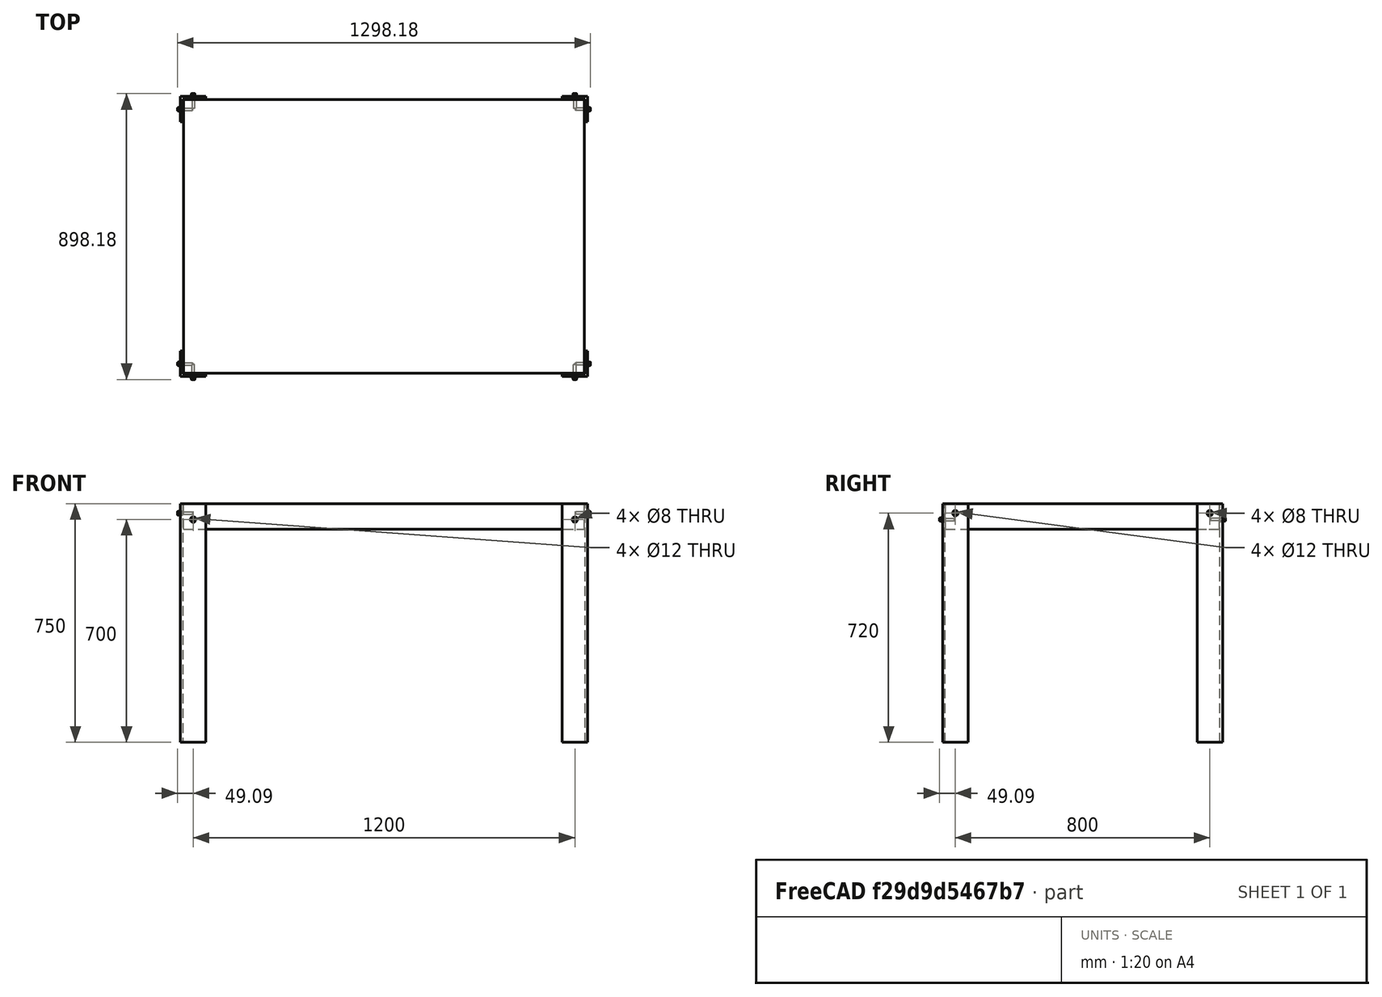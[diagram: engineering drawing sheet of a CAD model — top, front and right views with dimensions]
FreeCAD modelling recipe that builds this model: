
FCSTD DOCUMENT  (FreeCAD 0.16R6265 (Git))
Label: table
License: CreativeCommons Attribution
LicenseURL: http://creativecommons.org/licenses/by/4.0/
objects: Part::Cut×12, Part::Box×9, Part::FeaturePython×8, Part::Cylinder×4, App::DocumentObjectGroup×1
note: 33 computed .brp shape members not serialized (recipe doc carries the construction recipe); baked Part::Feature solids carry a one-line shape summary decoded from their .brp

FEATURE [Part::Box] Box  label="Cube"
  Height = 750
  Length = 80
  Width = 80
FEATURE [Part::Box] Box001  label="Cube001"
  Height = 750
  Length = 80
  Placement = pos=(8,8,0) rot=(0,0,1;0rad)
  Width = 80
FEATURE [Part::Cut] Cut
  Base = -> Box
  Tool = -> Box001
FEATURE [Part::Box] Box002  label="Cube002"
  Height = 750
  Length = 80
  Placement = pos=(0,800,0) rot=(0,0,1;0rad)
  Width = 80
FEATURE [Part::Box] Box003  label="Cube003"
  Height = 750
  Length = 80
  Placement = pos=(8,792,0) rot=(0,0,1;0rad)
  Width = 80
FEATURE [Part::Cut] Cut001
  Base = -> Box002
  Tool = -> Box003
FEATURE [Part::Box] Box004  label="Cube004"
  Height = 750
  Length = 80
  Placement = pos=(1200,0,0) rot=(0,0,1;0rad)
  Width = 80
FEATURE [Part::Box] Box005  label="Cube005"
  Height = 750
  Length = 80
  Placement = pos=(1192,8,0) rot=(0,0,1;0rad)
  Width = 80
FEATURE [Part::Cut] Cut002
  Base = -> Box004
  Tool = -> Box005
FEATURE [Part::Box] Box006  label="Cube006"
  Height = 750
  Length = 80
  Placement = pos=(1200,800,0) rot=(0,0,1;0rad)
  Width = 80
FEATURE [Part::Box] Box007  label="Cube007"
  Height = 750
  Length = 80
  Placement = pos=(1192,792,0) rot=(0,0,1;0rad)
  Width = 80
FEATURE [Part::Cut] Cut003
  Base = -> Box006
  Tool = -> Box007
FEATURE [Part::Box] Box008  label="Tabletop"
  Height = 80
  Length = 1260
  Placement = pos=(10,10,670) rot=(0,0,1;0rad)
  Width = 860
  expr: Width = 880 - 20
  expr: Length = 1280 - 20
FEATURE [Part::Cylinder] Cylinder
  Angle = 360
  Height = 1300
  Placement = pos=(-10,40,720) rot=(0,1,0;1.5708rad)
  Radius = 6
FEATURE [Part::Cylinder] Cylinder001
  Angle = 360
  Height = 1300
  Placement = pos=(-10,840,720) rot=(0,1,0;1.5708rad)
  Radius = 6
FEATURE [Part::Cylinder] Cylinder002
  Angle = 360
  Height = 900
  Placement = pos=(40,-10,700) rot=(-1,0,0;1.5708rad)
  Radius = 6
FEATURE [Part::Cylinder] Cylinder003
  Angle = 360
  Height = 900
  Placement = pos=(1240,-10,700) rot=(-1,0,0;1.5708rad)
  Radius = 6
FEATURE [Part::Cut] Cut004
  Base = -> Cut
  Tool = -> Cylinder
FEATURE [Part::Cut] Cut005
  Base = -> Cut002
  Tool = -> Cylinder
FEATURE [Part::Cut] Cut006  label="Foot 01"
  Base = -> Cut004
  Tool = -> Cylinder002
FEATURE [Part::Cut] Cut007
  Base = -> Cut001
  Tool = -> Cylinder002
FEATURE [Part::Cut] Cut008  label="Foot 02"
  Base = -> Cut007
  Tool = -> Cylinder001
FEATURE [Part::Cut] Cut009
  Base = -> Cut003
  Tool = -> Cylinder001
FEATURE [Part::Cut] Cut010  label="Foot 03"
  Base = -> Cut009
  Tool = -> Cylinder003
FEATURE [Part::Cut] Cut011  label="Foot 04"
  Base = -> Cut005
  Tool = -> Cylinder003
FEATURE [Part::FeaturePython] Screw  label="M8x40-Screw"  # Fasteners workbench fastener (typed FeaturePython)
  Placement = pos=(-2,40,720) rot=(0,-1,0;1.5708rad)
  diameter = 3
  invert = false
  length = 5
  matchOuter = false
  offset = 0
  thread = false
  type = 1
FEATURE [Part::FeaturePython] Screw001  label="M8x40-Screw001"  # Fasteners workbench fastener (typed FeaturePython)
  Placement = pos=(-2,840,720) rot=(0,-1,0;1.5708rad)
  diameter = 3
  invert = false
  length = 5
  matchOuter = false
  offset = 0
  thread = false
  type = 1
FEATURE [Part::FeaturePython] Screw002  label="M8x40-Screw002"  # Fasteners workbench fastener (typed FeaturePython)
  Placement = pos=(1282,40,720) rot=(0,1,0;1.5708rad)
  diameter = 3
  invert = false
  length = 5
  matchOuter = false
  offset = 0
  thread = false
  type = 1
FEATURE [Part::FeaturePython] Screw003  label="M8x40-Screw003"  # Fasteners workbench fastener (typed FeaturePython)
  Placement = pos=(1282,840,720) rot=(0,1,0;1.5708rad)
  diameter = 3
  invert = false
  length = 5
  matchOuter = false
  offset = 0
  thread = false
  type = 1
FEATURE [Part::FeaturePython] Screw004  label="M8x40-Screw007"  # Fasteners workbench fastener (typed FeaturePython)
  Placement = pos=(40,882,700) rot=(-1,0,0;1.5708rad)
  diameter = 3
  invert = false
  length = 5
  matchOuter = false
  offset = 0
  thread = false
  type = 1
FEATURE [Part::FeaturePython] Screw005  label="M8x40-Screw005"  # Fasteners workbench fastener (typed FeaturePython)
  Placement = pos=(1240,-2,700) rot=(1,0,0;1.5708rad)
  diameter = 3
  invert = false
  length = 5
  matchOuter = false
  offset = 0
  thread = false
  type = 1
FEATURE [Part::FeaturePython] Screw006  label="M8x40-Screw006"  # Fasteners workbench fastener (typed FeaturePython)
  Placement = pos=(40,-2,700) rot=(1,0,0;1.5708rad)
  diameter = 3
  invert = false
  length = 5
  matchOuter = false
  offset = 0
  thread = false
  type = 1
FEATURE [Part::FeaturePython] Screw007  label="M8x40-Screw008"  # Fasteners workbench fastener (typed FeaturePython)
  Placement = pos=(1240,882,700) rot=(-1,0,0;1.5708rad)
  diameter = 3
  invert = false
  length = 5
  matchOuter = false
  offset = 0
  thread = false
  type = 1
FEATURE [App::DocumentObjectGroup] Group  label="Screws"
  Group = -> [Screw,Screw001,Screw002,Screw003,Screw004,Screw005,Screw006,Screw007]
